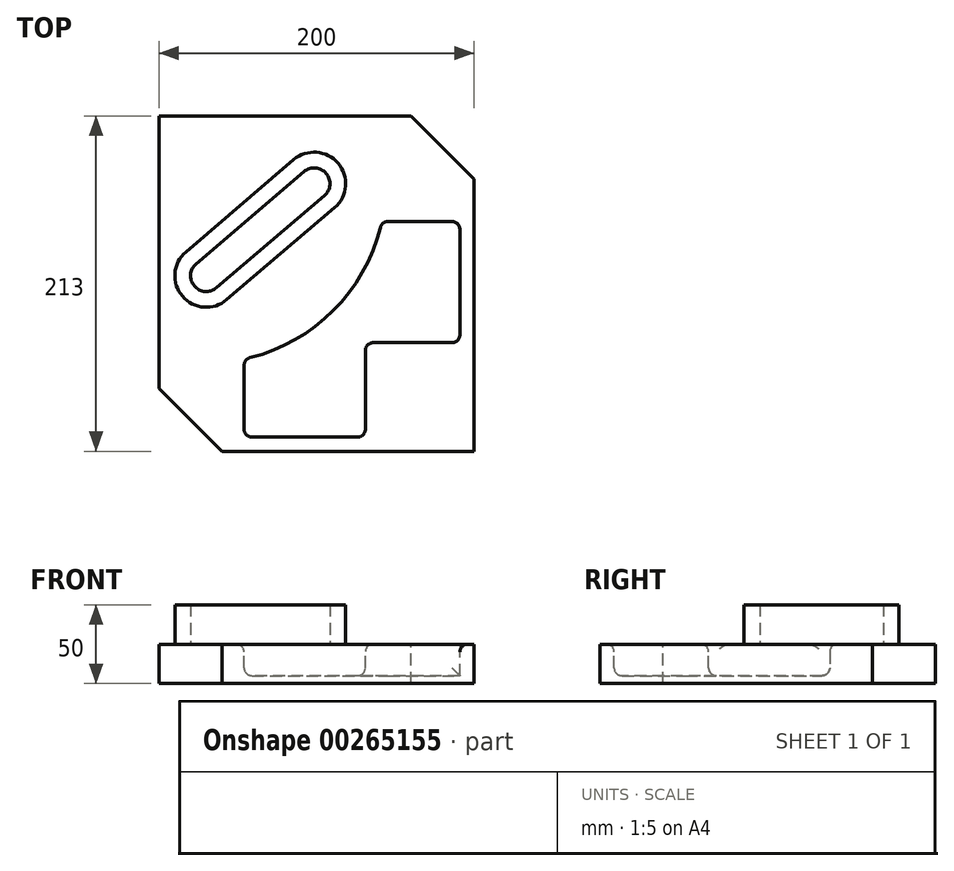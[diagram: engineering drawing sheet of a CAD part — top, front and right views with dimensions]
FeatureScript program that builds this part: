
annotation { "Feature Type Name" : "Feature", "Feature Type Description" : "" }
export const myFeature = defineFeature(function(context is Context, id is Id, definition is map)
    precondition{}
    {
        {
            var Q0;
            Q0=qCreatedBy(makeId("Top.planeOp"),FACE);
            var sketch = newSketch(context, id + "F0", { "sketchPlane" : qUnion([Q0])});
            skLineSegment(sketch, "E0", {"start": v(9.88, 0) * mm, "end": v(160, 0) * mm});
            skLineSegment(sketch, "E1", {"start": v(0, -11.6) * mm, "end": v(0, -173) * mm});
            skLineSegment(sketch, "E2", {"start": v(0, -173) * mm, "end": v(40, -213) * mm});
            skLineSegment(sketch, "E3", {"start": v(160, 0) * mm, "end": v(200, -40) * mm});
            skLineSegment(sketch, "E4", {"start": v(200, -40) * mm, "end": v(200, -213) * mm});
            skLineSegment(sketch, "E5", {"start": v(40, -213) * mm, "end": v(190.16, -213) * mm});
            skCircle(sketch, "E6", {"center": v(98.5, -43) * mm, "radius": 10 * mm});
            skCircle(sketch, "E7", {"center": v(98.5, -43) * mm, "radius": 20 * mm});
            skCircle(sketch, "E8", {"center": v(30, -101.5) * mm, "radius": 10 * mm});
            skCircle(sketch, "E9", {"center": v(30, -101.5) * mm, "radius": 20 * mm});
            skLineSegment(sketch, "E10", {"start": v(17, -86.3) * mm, "end": v(85.51, -27.79) * mm});
            skLineSegment(sketch, "E11", {"start": v(43, -116.71) * mm, "end": v(111.5, -58.21) * mm});
            skLineSegment(sketch, "E12", {"start": v(30, -203) * mm, "end": v(30, -101.5) * mm, "construction": true});
            skLineSegment(sketch, "E13", {"start": v(151.05, -40) * mm, "end": v(200, -40) * mm, "construction": true});
            skLineSegment(sketch, "E14", {"start": v(40, -213) * mm, "end": v(-38.27, -213) * mm, "construction": true});
            skArc(sketch, "E15", {"start": v(54, -154.45) * mm, "mid": v(110.6, -123.61) * mm, "end": v(141.44, -67) * mm});
            skLineSegment(sketch, "E16", {"start": v(141.44, -67) * mm, "end": v(191, -67) * mm});
            skLineSegment(sketch, "E17", {"start": v(191, -67) * mm, "end": v(191, -144) * mm});
            skLineSegment(sketch, "E18", {"start": v(191, -144) * mm, "end": v(131, -144) * mm});
            skLineSegment(sketch, "E19", {"start": v(131, -144) * mm, "end": v(131, -204) * mm});
            skLineSegment(sketch, "E20", {"start": v(131, -204) * mm, "end": v(54, -204) * mm});
            skLineSegment(sketch, "E21", {"start": v(54, -204) * mm, "end": v(54, -154.45) * mm});
            skLineSegment(sketch, "E22", {"start": v(23.5, -93.9) * mm, "end": v(92.01, -35.4) * mm});
            skLineSegment(sketch, "E23", {"start": v(36.5, -109.1) * mm, "end": v(105, -50.6) * mm});
            skPoint(sketch, "E24.end.orphan", {"position": v(200, -204.83) * mm});
            skLineSegment(sketch, "E25", {"start": v(0, -11.6) * mm, "end": v(0, 0) * mm});
            skLineSegment(sketch, "E26", {"start": v(0, 0) * mm, "end": v(9.88, 0) * mm});
            skLineSegment(sketch, "E27", {"start": v(190.16, -213) * mm, "end": v(200, -213) * mm});
            skSolve(sketch);
        }
        {
            var Q0;
            Q0=makeQuery(id+"F0.imprint","IMPRINT",FACE,{"disambiguationData":[TD([[makeQuery(id+"F0.imprint","IMPRINT",EDGE,{"derivedFrom":sQuery(id+"F0.wireOp",EDGE,"E0")}),-1.0]])]});
            var Q1;
            {var subQ0=sQuery(id+"F0.wireOp",EDGE,"E22");var subQ1=sQuery(id+"F0.wireOp",EDGE,"E7");var subQ2=makeQuery(id+"F0.imprint","INTERSECT",VERTEX,{"derivedFrom":[subQ1,subQ0]});Q1=makeQuery(id+"F0.imprint","IMPRINT",FACE,{"disambiguationData":[TD([[makeQuery(id+"F0.imprint","IMPRINT",EDGE,{"disambiguationData":[TD([[subQ2,-1.0]])],"derivedFrom":subQ1}),-1.0]])]});}
            var Q2;
            {var subQ0=sQuery(id+"F0.wireOp",EDGE,"E22");var subQ1=sQuery(id+"F0.wireOp",EDGE,"E8");var subQ2=makeQuery(id+"F0.imprint","INTERSECT",VERTEX,{"derivedFrom":[subQ1,subQ0]});Q2=makeQuery(id+"F0.imprint","IMPRINT",FACE,{"disambiguationData":[TD([[makeQuery(id+"F0.imprint","IMPRINT",EDGE,{"disambiguationData":[TD([[subQ2,1.0]])],"derivedFrom":subQ1}),-1.0]])]});}
            var Q3;
            {var subQ0=sQuery(id+"F0.wireOp",EDGE,"E8");var subQ1=makeQuery(id+"F0.imprint","INTERSECT",VERTEX,{"derivedFrom":[subQ0,sQuery(id+"F0.wireOp",EDGE,"E22")]});Q3=makeQuery(id+"F0.imprint","IMPRINT",FACE,{"disambiguationData":[TD([[makeQuery(id+"F0.imprint","IMPRINT",EDGE,{"disambiguationData":[TD([[subQ1,-1.0]])],"derivedFrom":subQ0}),1.0]])]});}
            var Q4;
            {var subQ5=sQuery(id+"F0.wireOp",EDGE,"E22");var subQ6=sQuery(id+"F0.wireOp",EDGE,"E8");var subQ7=makeQuery(id+"F0.imprint","INTERSECT",VERTEX,{"derivedFrom":[subQ6,subQ5]});Q4=makeQuery(id+"F0.imprint","IMPRINT",FACE,{"disambiguationData":[TD([[makeQuery(id+"F0.imprint","IMPRINT",EDGE,{"disambiguationData":[TD([[subQ7,-1.0]])],"derivedFrom":subQ6}),-1.0]])]});}
            var Q5;
            {var subQ0=sQuery(id+"F0.wireOp",EDGE,"E11");Q5=makeQuery(id+"F0.imprint","IMPRINT",FACE,{"disambiguationData":[TD([[makeQuery(id+"F0.imprint","IMPRINT",EDGE,{"derivedFrom":subQ0}),1.0]])]});}
            var Q6;
            {var subQ5=sQuery(id+"F0.wireOp",EDGE,"E22");var subQ7=sQuery(id+"F0.wireOp",EDGE,"E6");var subQ9=makeQuery(id+"F0.imprint","INTERSECT",VERTEX,{"derivedFrom":[subQ7,subQ5]});Q6=makeQuery(id+"F0.imprint","IMPRINT",FACE,{"disambiguationData":[TD([[makeQuery(id+"F0.imprint","IMPRINT",EDGE,{"disambiguationData":[TD([[subQ9,1.0]])],"derivedFrom":subQ7}),-1.0]])]});}
            var Q7;
            {var subQ0=sQuery(id+"F0.wireOp",EDGE,"E10");Q7=makeQuery(id+"F0.imprint","IMPRINT",FACE,{"disambiguationData":[TD([[makeQuery(id+"F0.imprint","IMPRINT",EDGE,{"derivedFrom":subQ0}),-1.0]])]});}
            var Q8;
            {var subQ0=sQuery(id+"F0.wireOp",EDGE,"E22");var subQ1=sQuery(id+"F0.wireOp",EDGE,"E6");var subQ2=makeQuery(id+"F0.imprint","INTERSECT",VERTEX,{"derivedFrom":[subQ1,subQ0]});Q8=makeQuery(id+"F0.imprint","IMPRINT",FACE,{"disambiguationData":[TD([[makeQuery(id+"F0.imprint","IMPRINT",EDGE,{"disambiguationData":[TD([[subQ2,-1.0]])],"derivedFrom":subQ1}),-1.0]])]});}
            var Q9;
            {var subQ0=sQuery(id+"F0.wireOp",EDGE,"E6");var subQ1=makeQuery(id+"F0.imprint","INTERSECT",VERTEX,{"derivedFrom":[subQ0,sQuery(id+"F0.wireOp",EDGE,"E22")]});Q9=makeQuery(id+"F0.imprint","IMPRINT",FACE,{"disambiguationData":[TD([[makeQuery(id+"F0.imprint","IMPRINT",EDGE,{"disambiguationData":[TD([[subQ1,-1.0]])],"derivedFrom":subQ0}),1.0]])]});}
            var Q10;
            Q10=makeQuery(id+"F0.imprint","IMPRINT",FACE,{"disambiguationData":[TD([[makeQuery(id+"F0.imprint","IMPRINT",EDGE,{"derivedFrom":sQuery(id+"F0.wireOp",EDGE,"E15")}),-1.0]])]});
            extrude(context, id + "F1", {"entities" : qUnion([Q0, Q1, Q2, Q3, Q4, Q5, Q6, Q7, Q8, Q9, Q10]), "oppositeDirection" : true, "depth" : 25 * mm});
        }
        {
            var Q0;
            {var subQ5=sQuery(id+"F0.wireOp",EDGE,"E22");var subQ7=sQuery(id+"F0.wireOp",EDGE,"E6");var subQ9=makeQuery(id+"F0.imprint","INTERSECT",VERTEX,{"derivedFrom":[subQ7,subQ5]});Q0=makeQuery(id+"F0.imprint","IMPRINT",FACE,{"disambiguationData":[TD([[makeQuery(id+"F0.imprint","IMPRINT",EDGE,{"disambiguationData":[TD([[subQ9,1.0]])],"derivedFrom":subQ7}),-1.0]])]});}
            var Q1;
            {var subQ0=sQuery(id+"F0.wireOp",EDGE,"E11");Q1=makeQuery(id+"F0.imprint","IMPRINT",FACE,{"disambiguationData":[TD([[makeQuery(id+"F0.imprint","IMPRINT",EDGE,{"derivedFrom":subQ0}),1.0]])]});}
            var Q2;
            {var subQ0=sQuery(id+"F0.wireOp",EDGE,"E10");Q2=makeQuery(id+"F0.imprint","IMPRINT",FACE,{"disambiguationData":[TD([[makeQuery(id+"F0.imprint","IMPRINT",EDGE,{"derivedFrom":subQ0}),-1.0]])]});}
            var Q3;
            {var subQ5=sQuery(id+"F0.wireOp",EDGE,"E22");var subQ6=sQuery(id+"F0.wireOp",EDGE,"E8");var subQ7=makeQuery(id+"F0.imprint","INTERSECT",VERTEX,{"derivedFrom":[subQ6,subQ5]});Q3=makeQuery(id+"F0.imprint","IMPRINT",FACE,{"disambiguationData":[TD([[makeQuery(id+"F0.imprint","IMPRINT",EDGE,{"disambiguationData":[TD([[subQ7,-1.0]])],"derivedFrom":subQ6}),-1.0]])]});}
            extrude(context, id + "F2", {"entities" : qUnion([Q0, Q1, Q2, Q3]), "operationType" : NewBodyOperationType.ADD, "depth" : 25 * mm});
        }
        {
            var Q0;
            Q0=makeQuery(id+"F0.imprint","IMPRINT",FACE,{"disambiguationData":[TD([[makeQuery(id+"F0.imprint","IMPRINT",EDGE,{"derivedFrom":sQuery(id+"F0.wireOp",EDGE,"E15")}),-1.0]])]});
            extrude(context, id + "F3", {"entities" : qUnion([Q0]), "operationType" : NewBodyOperationType.REMOVE, "oppositeDirection" : true, "depth" : 20 * mm});
        }
        {
            var Q0;
            Q0=makeQuery(id+"F3.boolean.opBoolean","COPY",FACE,{"derivedFrom":makeQuery(id+"F3.opExtrude","SWEPT_FACE",FACE,{"disambiguationData":[OSD([sQuery(id+"F0.wireOp",EDGE,"E15")])]})});
            var Q1;
            Q1=makeQuery(id+"F3.boolean.opBoolean","COPY",FACE,{"derivedFrom":makeQuery(id+"F3.opExtrude","SWEPT_FACE",FACE,{"disambiguationData":[OSD([sQuery(id+"F0.wireOp",EDGE,"E16")])]})});
            var Q2;
            Q2=makeQuery(id+"F3.boolean.opBoolean","COPY",FACE,{"derivedFrom":makeQuery(id+"F3.opExtrude","SWEPT_FACE",FACE,{"disambiguationData":[OSD([sQuery(id+"F0.wireOp",EDGE,"E19")])]})});
            var Q3;
            Q3=makeQuery(id+"F3.boolean.opBoolean","COPY",FACE,{"derivedFrom":makeQuery(id+"F3.opExtrude","SWEPT_FACE",FACE,{"disambiguationData":[OSD([sQuery(id+"F0.wireOp",EDGE,"E18")])]})});
            var Q4;
            Q4=makeQuery(id+"F3.boolean.opBoolean","COPY",FACE,{"derivedFrom":makeQuery(id+"F3.opExtrude","SWEPT_FACE",FACE,{"disambiguationData":[OSD([sQuery(id+"F0.wireOp",EDGE,"E21")])]})});
            var Q5;
            Q5=makeQuery(id+"F3.boolean.opBoolean","COPY",FACE,{"derivedFrom":makeQuery(id+"F3.opExtrude","SWEPT_FACE",FACE,{"disambiguationData":[OSD([sQuery(id+"F0.wireOp",EDGE,"E20")])]})});
            var Q6;
            Q6=makeQuery(id+"F2.opExtrude","CAP_EDGE",EDGE,{"disambiguationData":[OSD([sQuery(id+"F0.wireOp",EDGE,"E11")])],"isStart":true});
            fillet(context, id + "F4", {"entities" : qUnion([Q0, Q1, Q2, Q3, Q4, Q5, Q6]), "radius" : 5 * mm, "tangentPropagation" : true, "allowEdgeOverflow" : false});
        }
    });
